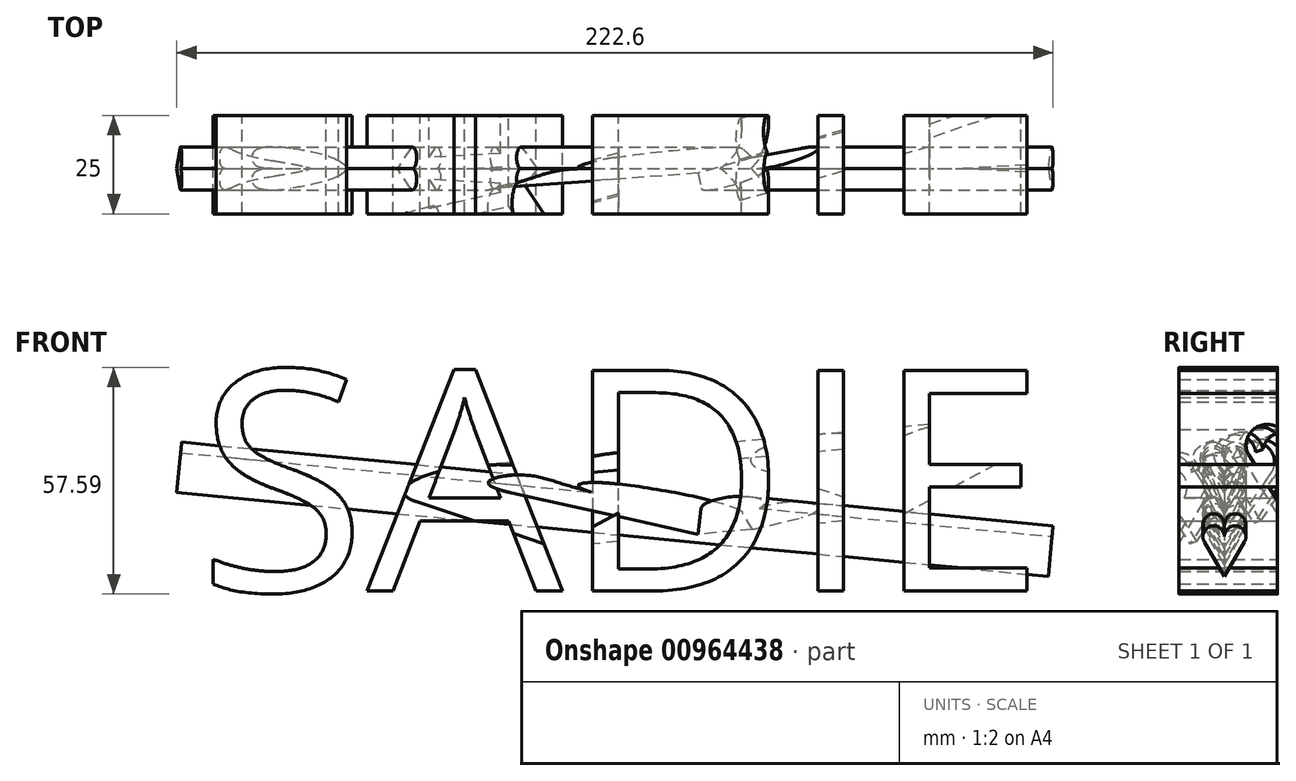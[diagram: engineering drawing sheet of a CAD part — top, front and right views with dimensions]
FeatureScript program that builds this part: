
annotation { "Feature Type Name" : "Feature", "Feature Type Description" : "" }
export const myFeature = defineFeature(function(context is Context, id is Id, definition is map)
    precondition{}
    {
        {
            var Q0;
            Q0=qCreatedBy(makeId("Front.planeOp"),FACE);
            var sketch = newSketch(context, id + "F0", { "sketchPlane" : qUnion([Q0])});
            skText(sketch, "E0", { "text": "SADIE", "fontName": "OpenSans-Regular.ttf"});
            skLineSegment(sketch, "E1", {"start": v(115.21, -13.74) * mm, "end": v(120.67, 43.09) * mm});
            const initialGuessF0  = {"E0": [-0.10059, -0.01374, 1, 0, 0.0565]};
            skSetInitialGuess(sketch, initialGuessF0);
            skSolve(sketch);
        }
        {
            var Q0;
            Q0=makeQuery(id+"F0.imprint","IMPRINT",FACE,{"disambiguationData":[TD([[makeQuery(id+"F0.imprint","IMPRINT",EDGE,{"derivedFrom":sQuery(id+"F0.wireOp",EDGE,"E0.sketch_text.stroke-0")}),-1.0]])]});
            var Q1;
            Q1=makeQuery(id+"F0.imprint","IMPRINT",FACE,{"disambiguationData":[TD([[makeQuery(id+"F0.imprint","IMPRINT",EDGE,{"derivedFrom":sQuery(id+"F0.wireOp",EDGE,"E0.sketch_text.stroke-25")}),-1.0]])]});
            var Q2;
            Q2=makeQuery(id+"F0.imprint","IMPRINT",FACE,{"disambiguationData":[TD([[makeQuery(id+"F0.imprint","IMPRINT",EDGE,{"derivedFrom":sQuery(id+"F0.wireOp",EDGE,"E0.sketch_text.stroke-38")}),-1.0]])]});
            var Q3;
            Q3=makeQuery(id+"F0.imprint","IMPRINT",FACE,{"disambiguationData":[TD([[makeQuery(id+"F0.imprint","IMPRINT",EDGE,{"derivedFrom":sQuery(id+"F0.wireOp",EDGE,"E0.sketch_text.stroke-52")}),-1.0]])]});
            var Q4;
            Q4=makeQuery(id+"F0.imprint","IMPRINT",FACE,{"disambiguationData":[TD([[makeQuery(id+"F0.imprint","IMPRINT",EDGE,{"derivedFrom":sQuery(id+"F0.wireOp",EDGE,"E0.sketch_text.stroke-56")}),-1.0]])]});
            extrude(context, id + "F1", {"entities" : qUnion([Q0, Q1, Q2, Q3, Q4]), "depth" : 25 * mm, "offsetDistance" : 25 * mm});
        }
        {
            var Q0;
            Q0=sQuery(id+"F0.wireOp",EDGE,"E1");
            cPlane(context, id + "F2", {"entities" : qUnion([Q0]), "cplaneType" : CPlaneType.LINE_ANGLE, "offset" : 25 * mm, "angle" : 0 * degree, "width" : 150 * mm, "height" : 150 * mm});
        }
        {
            var Q0;
            Q0=qCreatedBy(id+"F2.planeOp",FACE);
            var sketch = newSketch(context, id + "F3", { "sketchPlane" : qUnion([Q0])});
            skArc(sketch, "E2", {"start": v(-13.46, 11.26) * mm, "mid": v(-16.9, 13.9) * mm, "end": v(-18.55, 9.89) * mm});
            skLineSegment(sketch, "E3", {"start": v(-13.46, 1.1) * mm, "end": v(-18.55, 9.89) * mm});
            skLineSegment(sketch, "E4.MirrorCS", {"start": v(-12.46, -61.87) * mm, "end": v(-17.55, -70.64) * mm});
            skArc(sketch, "E5.MirrorCS", {"start": v(-13.46, 11.26) * mm, "mid": v(-10.01, 13.9) * mm, "end": v(-8.36, 9.89) * mm});
            skLineSegment(sketch, "E6.MirrorCS", {"start": v(-13.46, 1.1) * mm, "end": v(-8.36, 9.89) * mm});
            skSolve(sketch);
        }
        {
            var Q0;
            Q0=makeQuery(id+"F3.imprint","IMPRINT",FACE,{"disambiguationData":[TD([[makeQuery(id+"F3.imprint","IMPRINT",EDGE,{"derivedFrom":sQuery(id+"F3.wireOp",EDGE,"E2")}),1.0]])]});
            extrude(context, id + "F4", {"entities" : qUnion([Q0]), "operationType" : NewBodyOperationType.REMOVE, "endBound" : BoundingType.THROUGH_ALL, "oppositeDirection" : true, "depth" : 25 * mm, "offsetDistance" : 25 * mm});
        }
        {
            var Q0;
            Q0=makeQuery(id+"F3.imprint","IMPRINT",FACE,{"disambiguationData":[TD([[makeQuery(id+"F3.imprint","IMPRINT",EDGE,{"derivedFrom":sQuery(id+"F3.wireOp",EDGE,"E2")}),1.0]])]});
            extrude(context, id + "F5", {"entities" : qUnion([Q0]), "endBound" : BoundingType.THROUGH_ALL, "oppositeDirection" : true, "depth" : 70 * mm, "offsetDistance" : 25 * mm});
        }
        {
            var Q0;
            Q0=qCreatedBy(makeId("Top.planeOp"),FACE);
            var sketch = newSketch(context, id + "F6", { "sketchPlane" : qUnion([Q0])});
            skLineSegment(sketch, "E7", {"start": v(-109.1, -38.97) * mm, "end": v(-98.95, -74.7) * mm});
            skSolve(sketch);
        }
        {
            var Q0;
            Q0=sQuery(id+"F6.wireOp",EDGE,"E7");
            cPlane(context, id + "F7", {"entities" : qUnion([Q0]), "cplaneType" : CPlaneType.LINE_ANGLE, "offset" : 25 * mm, "angle" : 85 * degree, "oppositeDirection" : true, "width" : 150 * mm, "height" : 150 * mm});
        }
        {
            var Q0;
            Q0=qCreatedBy(id+"F7.planeOp",FACE);
            var sketch = newSketch(context, id + "F8", { "sketchPlane" : qUnion([Q0])});
            skLineSegment(sketch, "E8", {"start": v(21.35, 24.28) * mm, "end": v(21.35, -1.76) * mm, "construction": true});
            skArc(sketch, "E9", {"start": v(21.35, 16.37) * mm, "mid": v(14.62, 20.42) * mm, "end": v(12.08, 13) * mm});
            skLineSegment(sketch, "E10", {"start": v(12.08, 13) * mm, "end": v(21.35, -1.76) * mm});
            skArc(sketch, "E11.MirrorCS", {"start": v(21.35, 16.37) * mm, "mid": v(28.08, 20.42) * mm, "end": v(30.62, 13) * mm});
            skLineSegment(sketch, "E12.MirrorCS", {"start": v(30.62, 13) * mm, "end": v(21.35, -1.76) * mm});
            skSolve(sketch);
        }
        {
            var Q0;
            Q0 = qSketchRegion(id + "F8", true);
            var Q1;
            Q1 = qConstructionFilter(qBodyType(qCreatedBy(id + "F8" ,EDGE), BodyType.WIRE), ConstructionObject.NO);
            var Q2;
            Q2=makeQuery(id+"F5.opExtrude","SWEPT_BODY",BODY,{"disambiguationData":[OSD([sQuery(id+"F3.wireOp",EDGE,"E2"),sQuery(id+"F3.wireOp",EDGE,"E3"),sQuery(id+"F3.wireOp",EDGE,"E5.MirrorCS"),sQuery(id+"F3.wireOp",EDGE,"E6.MirrorCS")])]});
            extrude(context, id + "F9", {"entities" : qUnion([Q0]), "operationType" : NewBodyOperationType.REMOVE, "surfaceOperationType" : NewSurfaceOperationType.ADD, "surfaceEntities" : qUnion([Q1]), "endBound" : BoundingType.THROUGH_ALL, "oppositeDirection" : true, "depth" : 25 * mm, "endBoundEntityBody" : qUnion([Q2]), "offsetDistance" : 25 * mm});
        }
    });
